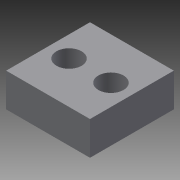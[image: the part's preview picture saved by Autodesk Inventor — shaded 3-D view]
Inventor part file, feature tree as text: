
AUTODESK INVENTOR PART (.ipt)
format: ipt  version: 2015 SP1 (Build 190203100, 203)  size: 75,264 bytes
history: native  units: mm
features: reference x5, other x1, extrude x1, sketch x1
ambient origin geometry x8: Origin, YZ Plane, XZ Plane, XY Plane, X Axis, Y Axis, Z Axis, Center Point
bodies: Body1 (feature_tree)
feature tree (8):
  other  "Sólido1"
  extrude  "Extrusión1"  [1 undecoded]
  sketch  "Boceto1"  dims[d0=4.0mm d1=0.0mm]
  reference  "Referencia1"
  reference  "Referencia2"
  reference  "Referencia3"
  reference  "Referencia4"
  reference  "Referencia5"
note: 1 required parameter value undecoded (feature->parameter linkage not recoverable at this tier; creation-order binding heuristic only, values carry confidence <= 0.55)
